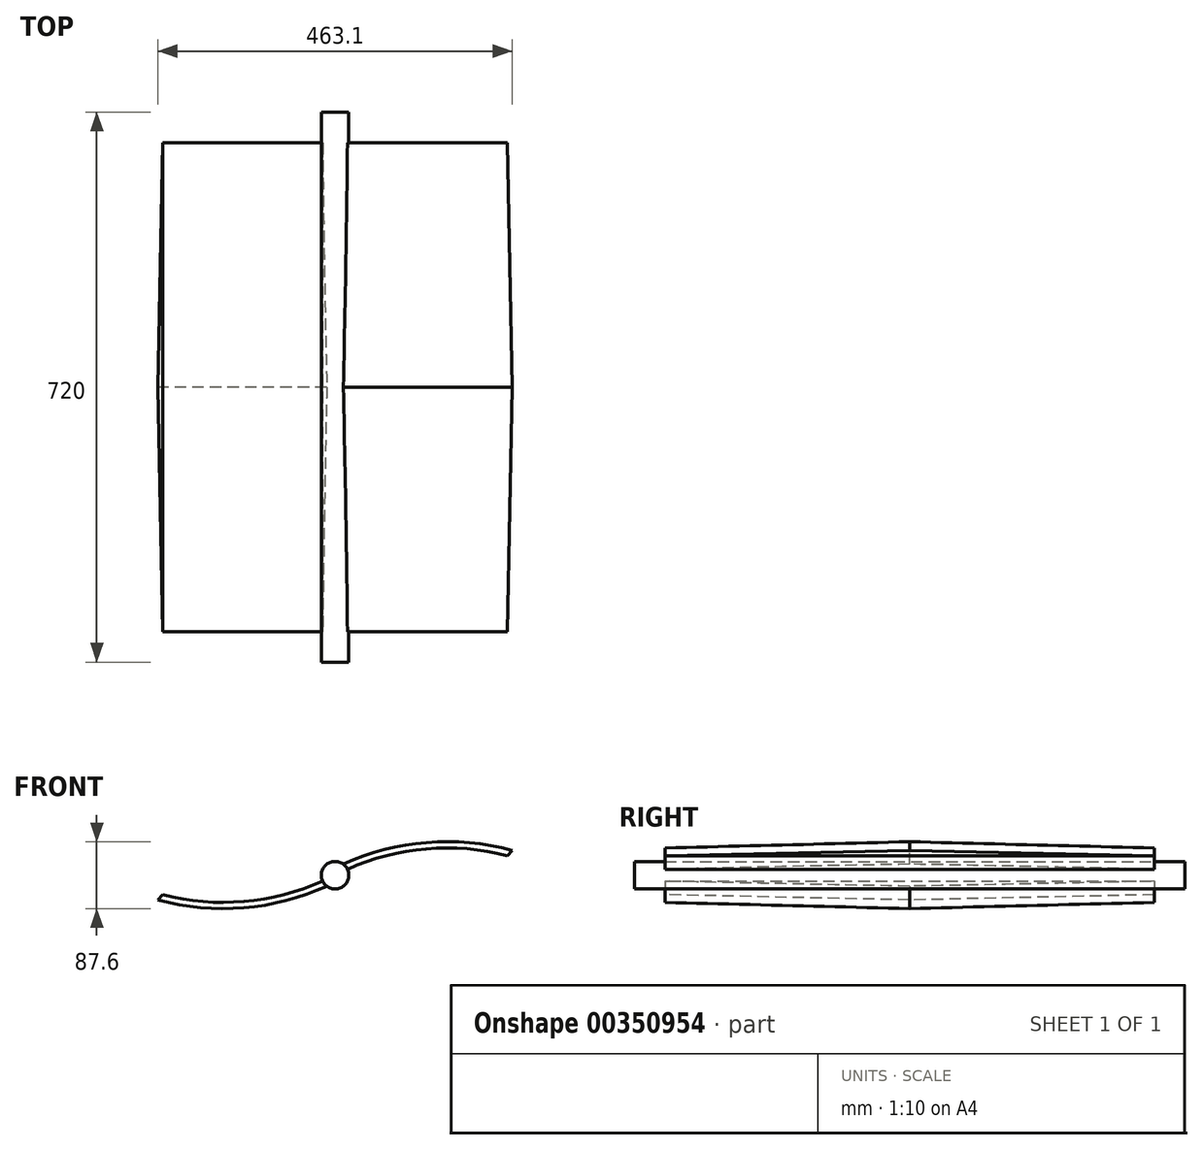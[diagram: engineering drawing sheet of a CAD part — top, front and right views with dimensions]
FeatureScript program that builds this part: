
annotation { "Feature Type Name" : "Feature", "Feature Type Description" : "" }
export const myFeature = defineFeature(function(context is Context, id is Id, definition is map)
    precondition{}
    {
        {
            var Q0;
            Q0=qCreatedBy(makeId("Front.planeOp"),FACE);
            var sketch = newSketch(context, id + "F0", { "sketchPlane" : qUnion([Q0])});
            skCircle(sketch, "E0", {"center": v(0, 0) * mm, "radius": 18 * mm});
            skArc(sketch, "E1", {"start": v(242.75, 20.74) * mm, "mid": v(128.28, 35.2) * mm, "end": v(16.17, 7.91) * mm});
            skArc(sketch, "E2.MirrorCS", {"start": v(-242.75, -20.74) * mm, "mid": v(-128.28, -35.2) * mm, "end": v(-16.17, -7.91) * mm});
            skSolve(sketch);
        }
        {
            var Q0;
            Q0=qCreatedBy(makeId("Right.planeOp"),FACE);
            var sketch = newSketch(context, id + "F1", { "sketchPlane" : qUnion([Q0])});
            skLineSegment(sketch, "E3", {"start": v(0, 0) * mm, "end": v(-320, 0) * mm});
            skLineSegment(sketch, "E4", {"start": v(0, 0) * mm, "end": v(320, 0) * mm});
            skLineSegment(sketch, "E5", {"start": v(320, 0) * mm, "end": v(0, 9.2) * mm});
            skLineSegment(sketch, "E6", {"start": v(0, 9.2) * mm, "end": v(-320, 0) * mm});
            skLineSegment(sketch, "E7.MirrorCS", {"start": v(0, -9.2) * mm, "end": v(-320, 0) * mm});
            skLineSegment(sketch, "E8.MirrorCS", {"start": v(320, 0) * mm, "end": v(0, -9.2) * mm});
            skSolve(sketch);
        }
        {
            var Q0;
            Q0=makeQuery(id+"F1.imprint","IMPRINT",FACE,{"disambiguationData":[TD([[makeQuery(id+"F1.imprint","IMPRINT",EDGE,{"derivedFrom":sQuery(id+"F1.wireOp",EDGE,"E3")}),-1.0]])]});
            var Q1;
            Q1=sQuery(id+"F0.wireOp",EDGE,"E1");
            sweep(context, id + "F2", {"profiles" : qUnion([Q0]), "path" : qUnion([Q1])});
        }
        {
            var Q0;
            Q0=makeQuery(id+"F1.imprint","IMPRINT",FACE,{"disambiguationData":[TD([[makeQuery(id+"F1.imprint","IMPRINT",EDGE,{"derivedFrom":sQuery(id+"F1.wireOp",EDGE,"E3")}),1.0]])]});
            var Q1;
            Q1=sQuery(id+"F0.wireOp",EDGE,"E2.MirrorCS");
            sweep(context, id + "F3", {"profiles" : qUnion([Q0]), "path" : qUnion([Q1])});
        }
        {
            var Q0;
            {var subQ0=sQuery(id+"F0.wireOp",EDGE,"E0");var subQ1=makeQuery(id+"F0.imprint","IMPRINT",VERTEX,{"disambiguationData":[OD(0.0)],"derivedFrom":subQ0});Q0=makeQuery(id+"F0.imprint","IMPRINT",FACE,{"disambiguationData":[TD([[makeQuery(id+"F0.imprint","IMPRINT",EDGE,{"disambiguationData":[TD([[subQ1,-1.0]])],"derivedFrom":subQ0}),1.0]])]});}
            extrude(context, id + "F4", {"entities" : qUnion([Q0]), "operationType" : NewBodyOperationType.ADD, "endBound" : BoundingType.SYMMETRIC, "depth" : 720 * mm});
        }
    });
